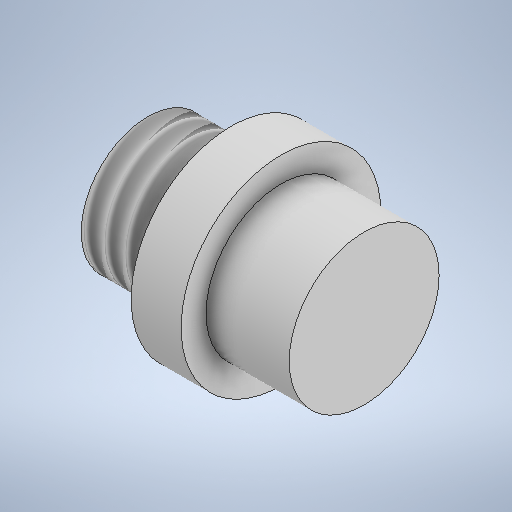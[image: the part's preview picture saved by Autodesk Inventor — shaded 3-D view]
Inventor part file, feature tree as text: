
AUTODESK INVENTOR PART (.ipt)
format: ipt  version: 2025.1 (Build 291241000, 241)  size: 270,336 bytes
history: native  units: mm
features: sketch x2, revolve x1, thread x1, plane x1
ambient origin geometry x8: Origin, YZ Plane, XZ Plane, XY Plane, X Axis, Y Axis, Z Axis, Center Point
bodies: Solid1 (feature_tree)
feature tree (5):
  revolve  "Revolution1"  [1 undecoded]
  thread  "Thread1"  [1 undecoded]
  plane  "Work Plane1"
  sketch  "Sketch2"  dims[d3=5.0mm d4=3.0mm d5=12.0mm d6=90.0deg d7=10.0mm d8=0.0mm d9=4.5mm]
  sketch  "Sketch1"  dims[d0=9.0mm d1=8.0mm d2=5.0mm]
note: 2 required parameter values undecoded (feature->parameter linkage not recoverable at this tier; creation-order binding heuristic only, values carry confidence <= 0.55)